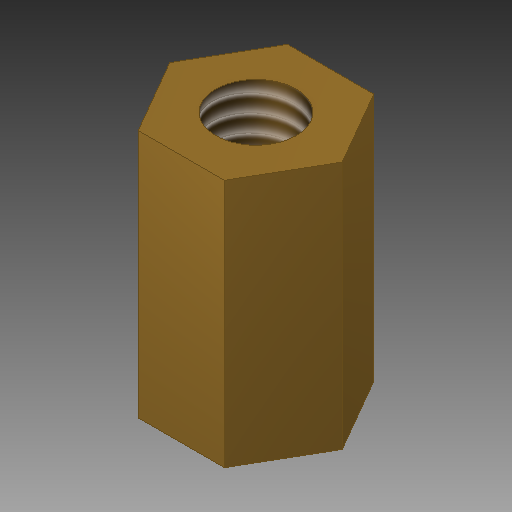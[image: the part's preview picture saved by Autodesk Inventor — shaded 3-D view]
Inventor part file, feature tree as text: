
AUTODESK INVENTOR PART (.ipt)
format: ipt  version: 2018 (Build 220112000, 112)  size: 114,688 bytes
history: native  units: mm
features: sketch x2, extrude x1, hole x1
ambient origin geometry x8: Origin, YZ Plane, XZ Plane, XY Plane, X Axis, Y Axis, Z Axis, Center Point
bodies: Solid1 (feature_tree)
feature tree (4):
  extrude  "Extrusion1"  Depth=10.0mm TaperAngle=0.0deg
  hole  "Hole1"  [1 undecoded]
  sketch  "Sketch1"  dims[d0=3.0mm d1=10.0mm d2=0.0mm]
  sketch  "Sketch2"  dims[d3=3.242mm d4=8.0mm d5=4.0mm d6=2.0mm d7=90.0deg d8=8.0mm d9=20.594885mm]
note: 1 required parameter value undecoded (feature->parameter linkage not recoverable at this tier; creation-order binding heuristic only, values carry confidence <= 0.55)
